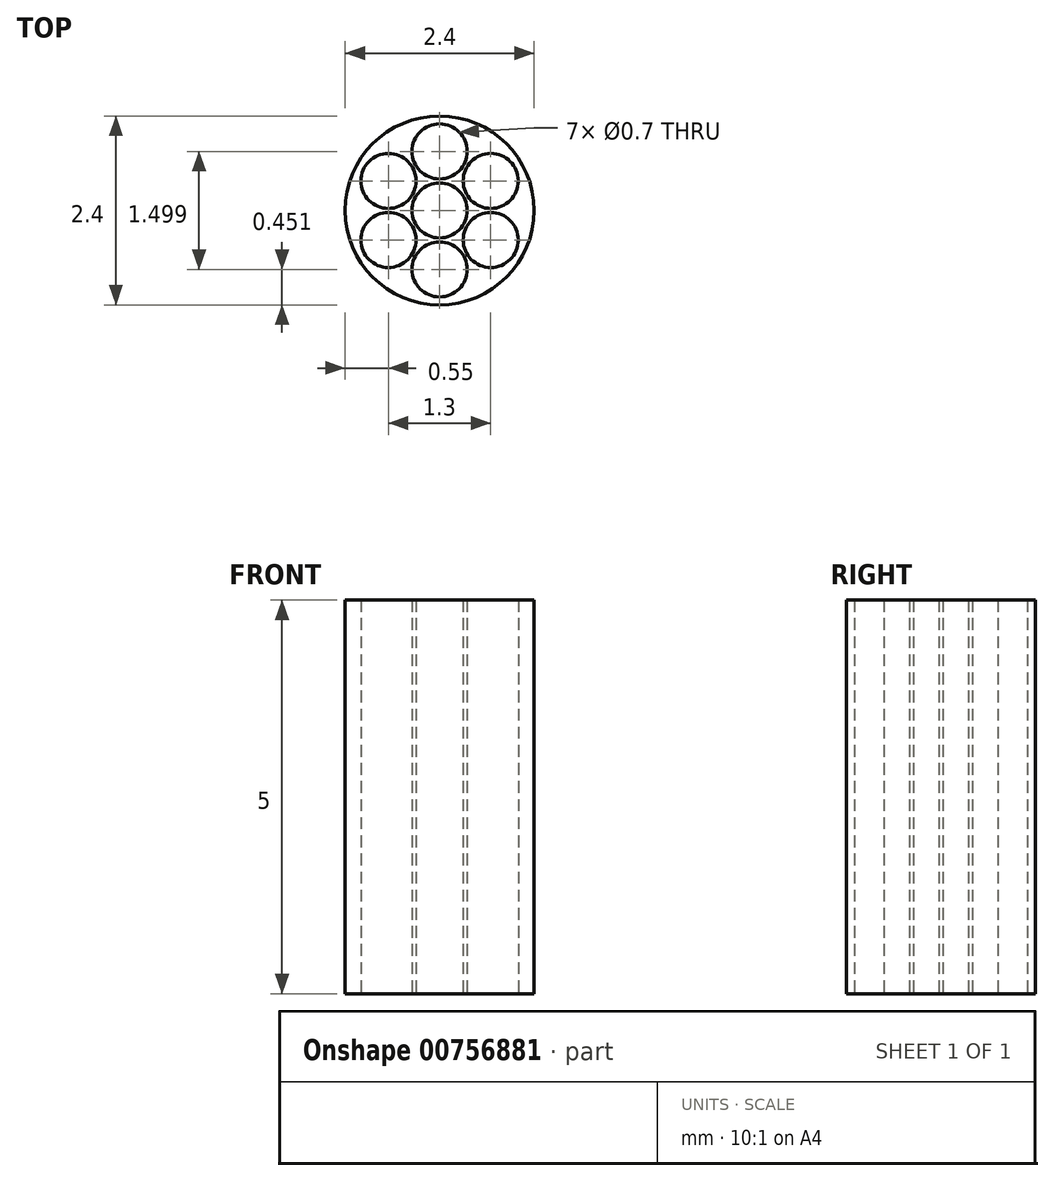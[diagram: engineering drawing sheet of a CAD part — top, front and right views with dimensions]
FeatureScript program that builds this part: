
annotation { "Feature Type Name" : "Feature", "Feature Type Description" : "" }
export const myFeature = defineFeature(function(context is Context, id is Id, definition is map)
    precondition{}
    {
        {
            var Q0;
            Q0=qCreatedBy(makeId("Top.planeOp"),FACE);
            var sketch = newSketch(context, id + "F0", { "sketchPlane" : qUnion([Q0])});
            skCircle(sketch, "E0", {"center": v(0, 0) * mm, "radius": 0.35 * mm});
            skCircle(sketch, "E1", {"center": v(0, 0.75) * mm, "radius": 0.35 * mm});
            skCircle(sketch, "E2", {"center": v(0.65, 0.38) * mm, "radius": 0.35 * mm});
            skCircle(sketch, "E3", {"center": v(0.65, -0.38) * mm, "radius": 0.35 * mm});
            skCircle(sketch, "E4", {"center": v(0, -0.75) * mm, "radius": 0.35 * mm});
            skCircle(sketch, "E5", {"center": v(-0.65, -0.38) * mm, "radius": 0.35 * mm});
            skCircle(sketch, "E6", {"center": v(-0.65, 0.38) * mm, "radius": 0.35 * mm});
            skSolve(sketch);
        }
        {
            var Q0;
            Q0=qCreatedBy(makeId("Top.planeOp"),FACE);
            var sketch = newSketch(context, id + "F1", { "sketchPlane" : qUnion([Q0])});
            skCircle(sketch, "E7", {"center": v(0, 0) * mm, "radius": 1.2 * mm});
            skSolve(sketch);
        }
        {
            var Q0;
            Q0=qSketchRegion(id+"F1",true);
            extrude(context, id + "F2", {"entities" : qUnion([Q0]), "depth" : 5 * mm, "offsetDistance" : 25 * mm});
        }
        {
            var Q0;
            Q0=qSketchRegion(id+"F0",true);
            extrude(context, id + "F3", {"entities" : qUnion([Q0]), "operationType" : NewBodyOperationType.REMOVE, "endBound" : BoundingType.THROUGH_ALL, "depth" : 25 * mm, "offsetDistance" : 25 * mm});
        }
    });
